# Revit family: _Camera-Security-Panasonic-360-degree-Indoor-Dome-Network-X4173Series
name_source: partatom
category: Security Devices
units: mm (PartAtom-declared; Revit-internal decimal feet)

## family parameters
Cut with Voids When Loaded = No
Host = Face
Maintain Annotation Orientation = No
OmniClass Number = 23.85.10.14.11
OmniClass Title = Cameras
Part Type = Normal
Room Calculation Point = No
Round Connector Dimension = Use Diameter
Shared = No

## types (4) — shared parameters
Angle Of View = 183
Communication Ports = 10Base-T / 100Base-TX, RJ45 connector
Equipment Abbreviation = SC
Family Version = 1.0.0
Focal Length = 0.055 "
Has POE = Yes
Height_Offset5 = 1.447 "
IP Or Analog = IP
Indoor Or Outdoor = Indoor
Manufacturer = Panasonic
Minimum Illumination = 0 lx
Model Disclaimer = Contact Panasonic for more information
Mounting Positions = Mount Dependent or Surface Mount
Operational Humidity = 10% to 90% (no condensation)
Product Material = Paint - Panasonic - Sail White
Product Page URL = https://security.panasonic.com
Provide Feedback = https://www.surveymonkey.com
Regulatory Compliance = UL (UL60950-1), c-UL (CSA C22.2 No.60950-1), CE, IEC60950-1 FCC (Part15 ClassA), ICES003 ClassA, EN55022 ClassB, EN55024
Scanning Area H = 0.218 "
Scanning Area V = 0.218 "
Storage Temperature = -22 °F to 140 °F
URL = http://security.panasonic.com
Vandal Resistant = No
Wide Dynamic Range = Yes
z Base Raduius = 3.228 "
z Horizontal FOV = 183.00°
z Vertical FOV = 183.00°
zero-valued in all types: Default Elevation, z Base Height

## per-type parameters (varying)
| type | Alarm Input Or Output Specification | Audio In | Audio Out | Date Last Modified | Description | Operational Temperature | Part Description | Power Active | Product Documentation Link | Voltage DC |
| WV-X4170 | No | No | No | 2018/01/12 | Security Camera, H.264/H.265 360-degree, Indoor, Dome, 9 Megapixel, Network, X4170 | 32°F to 104°F | Security Camera, H.264/H.265 360-degree, Indoor, Dome, 9 Megapixel, Network, X4170 | 7.2 W | http://ssbu-t.psn-web.net | 48 V |
| WV-X4171 | ALARM IN 1 (Auto time adjustment) (x1),ALARM IN 2 (ALARM OUT) (x1), ALARM IN 3 (AUX OUT) (x1) | 3.5 mm stereo mini jack | 3.5 mm stereo mini jack | 2018/01/15 | Security Camera, H.264/H.265 360-degree, Indoor, Dome, 9 Megapixel, Network, X4171 | 14°F to 122°F | Security Camera, H.264/H.265 360-degree, Indoor, Dome, 9 Megapixel, Network, X4171 | 6.7 W | http://ssbu-t.psn-web.net | 12 V |
| WV-X4172 | ALARM IN 1 (Auto time adjustment) (x1),ALARM IN 2 (ALARM OUT) (x1), ALARM IN 3 (AUX OUT) (x1) | 3.5 mm stereo mini jack | 3.5 mm stereo mini jack | 2020/10/28 | Security Camera, H.264/H.265 360-degree, Indoor, Dome, 9 Megapixel, Network, X4172 | 14°F to 122°F | Security Camera, H.264/H.265 360-degree, Indoor, Dome, 9 Megapixel, Network, X4172 | 6.7 W | https://bizpartner.panasonic.net | 12 V |
| WV-X4173 | ALARM IN 1 (Auto time adjustment) (x1),ALARM IN 2 (ALARM OUT) (x1), ALARM IN 3 (AUX OUT) (x1) | 3.5 mm stereo mini jack | 3.5 mm stereo mini jack | 2020/10/28 | Security Camera, H.264/H.265 360-degree, Indoor, Dome, 9 Megapixel, Network, X4173 | 14°F to 122°F | Security Camera, H.264/H.265 360-degree, Indoor, Dome, 9 Megapixel, Network, X4173 | 6.7 W | https://bizpartner.panasonic.net | 12 V |

note: column(s) folded — value = type name in every type: Model, Part Number

## geometry (parser evidence)
native form markers: Blend x2, Sweep x4
no freeform markers — native parametric forms only
